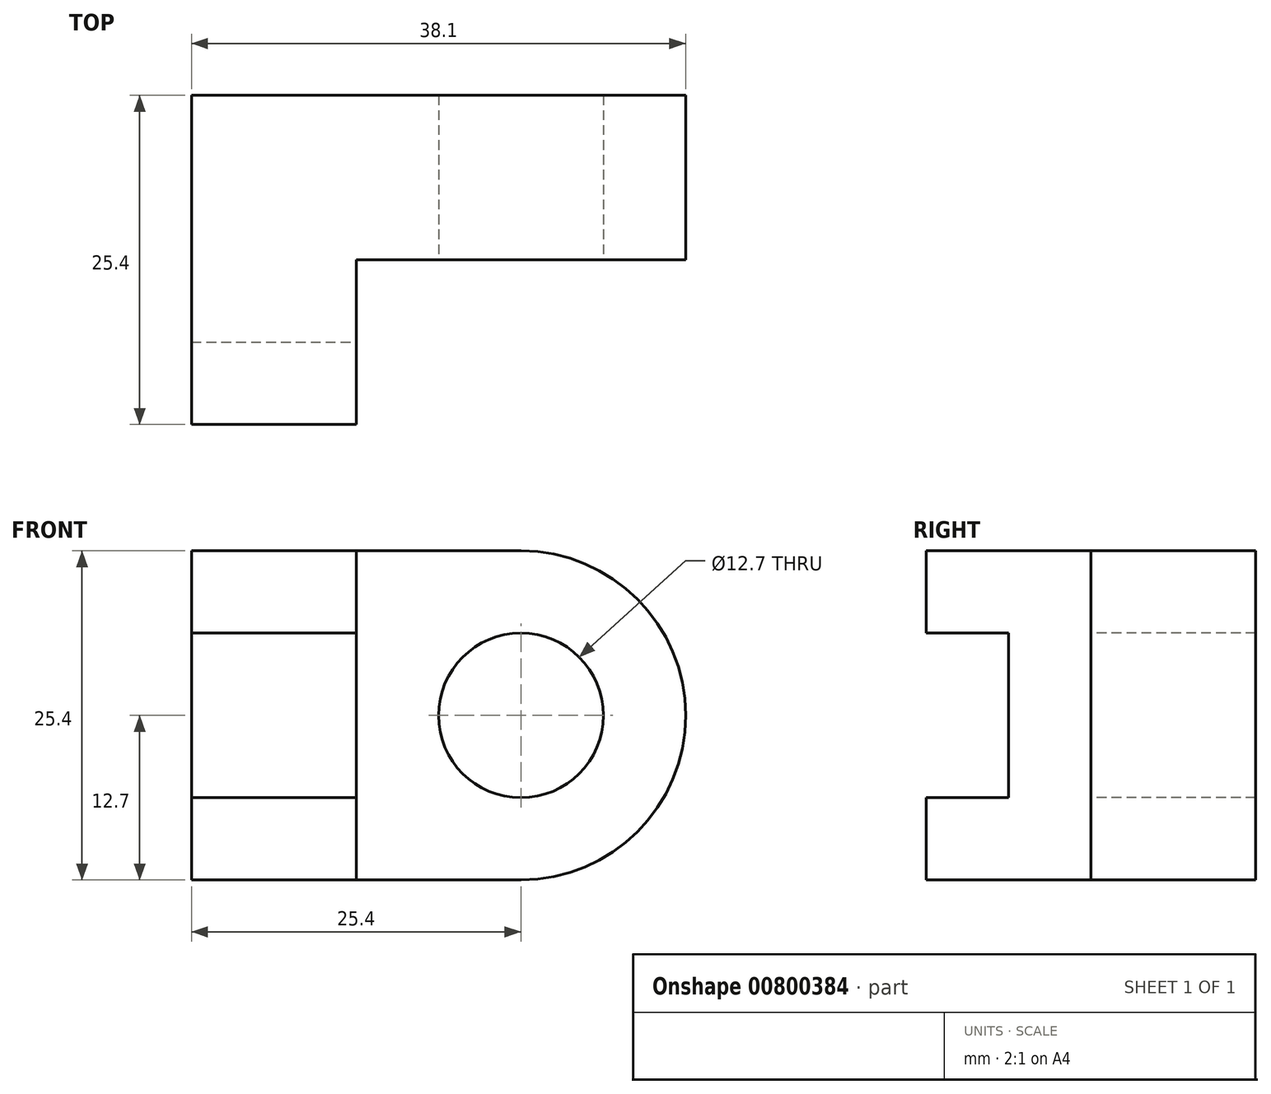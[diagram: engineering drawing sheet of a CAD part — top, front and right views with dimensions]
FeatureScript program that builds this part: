
annotation { "Feature Type Name" : "Feature", "Feature Type Description" : "" }
export const myFeature = defineFeature(function(context is Context, id is Id, definition is map)
    precondition{}
    {
        {
            var Q0;
            Q0=qCreatedBy(makeId("Top.planeOp"),FACE);
            var sketch = newSketch(context, id + "F0", { "sketchPlane" : qUnion([Q0])});
            skLineSegment(sketch, "E0", {"start": v(0, 0) * mm, "end": v(12.7, 0) * mm});
            skLineSegment(sketch, "E1", {"start": v(12.7, 0) * mm, "end": v(12.7, 12.7) * mm});
            skLineSegment(sketch, "E2", {"start": v(0, 0) * mm, "end": v(0, 25.4) * mm});
            skLineSegment(sketch, "E3", {"start": v(0, 25.4) * mm, "end": v(50.8, 25.4) * mm});
            skLineSegment(sketch, "E4", {"start": v(50.8, 25.4) * mm, "end": v(50.8, 12.7) * mm});
            skLineSegment(sketch, "E5", {"start": v(50.8, 12.7) * mm, "end": v(12.7, 12.7) * mm});
            skSolve(sketch);
        }
        {
            var Q0;
            Q0=makeQuery(id+"F0.imprint","IMPRINT",FACE,{"disambiguationData":[TD([[makeQuery(id+"F0.imprint","IMPRINT",EDGE,{"derivedFrom":sQuery(id+"F0.wireOp",EDGE,"E0")}),1.0]])]});
            extrude(context, id + "F1", {"entities" : qUnion([Q0]), "depth" : 25.4 * mm, "offsetDistance" : 25.4 * mm});
        }
        {
            var Q0;
            Q0=makeQuery(id+"F1.opExtrude","SWEPT_FACE",FACE,{"disambiguationData":[OSD([sQuery(id+"F0.wireOp",EDGE,"E1")])]});
            var sketch = newSketch(context, id + "F2", { "sketchPlane" : qUnion([Q0])});
            skLineSegment(sketch, "E6", {"start": v(0, 25.4) * mm, "end": v(0, 19.05) * mm});
            skLineSegment(sketch, "E7", {"start": v(0, 19.05) * mm, "end": v(6.35, 19.05) * mm});
            skLineSegment(sketch, "E8", {"start": v(6.35, 19.05) * mm, "end": v(6.35, 6.35) * mm});
            skLineSegment(sketch, "E9", {"start": v(6.35, 6.35) * mm, "end": v(0, 6.35) * mm});
            skSolve(sketch);
        }
        {
            var Q0;
            {var subQ0=sQuery(id+"F2.wireOp",EDGE,"E7");Q0=makeQuery(id+"F2.imprint","IMPRINT",FACE,{"disambiguationData":[TD([[makeQuery(id+"F2.imprint","IMPRINT",EDGE,{"derivedFrom":subQ0}),-1.0]])]});}
            extrude(context, id + "F3", {"entities" : qUnion([Q0]), "operationType" : NewBodyOperationType.REMOVE, "endBound" : BoundingType.THROUGH_ALL, "oppositeDirection" : true, "depth" : 25.4 * mm, "offsetDistance" : 25.4 * mm});
        }
        {
            var Q0;
            Q0=makeQuery(id+"F1.opExtrude","SWEPT_FACE",FACE,{"disambiguationData":[OSD([sQuery(id+"F0.wireOp",EDGE,"E5")])]});
            var sketch = newSketch(context, id + "F4", { "sketchPlane" : qUnion([Q0])});
            skLineSegment(sketch, "E10", {"start": v(12.7, 25.4) * mm, "end": v(25.4, 25.4) * mm});
            skLineSegment(sketch, "E11", {"start": v(12.7, 0) * mm, "end": v(25.4, 0) * mm});
            skArc(sketch, "E12", {"start": v(25.4, 0) * mm, "mid": v(38.1, 12.7) * mm, "end": v(25.4, 25.4) * mm});
            skCircle(sketch, "E13", {"center": v(25.4, 12.7) * mm, "radius": 6.35 * mm});
            skSolve(sketch);
        }
        {
            var Q0;
            {var subQ0=sQuery(id+"F4.wireOp",EDGE,"E12");Q0=makeQuery(id+"F4.imprint","IMPRINT",FACE,{"disambiguationData":[TD([[makeQuery(id+"F4.imprint","IMPRINT",EDGE,{"derivedFrom":subQ0}),-1.0]])]});}
            var Q1;
            Q1=makeQuery(id+"F4.imprint","IMPRINT",FACE,{"disambiguationData":[TD([[makeQuery(id+"F4.imprint","IMPRINT",EDGE,{"derivedFrom":sQuery(id+"F4.wireOp",EDGE,"E13")}),1.0]])]});
            extrude(context, id + "F5", {"entities" : qUnion([Q0, Q1]), "operationType" : NewBodyOperationType.REMOVE, "endBound" : BoundingType.THROUGH_ALL, "oppositeDirection" : true, "depth" : 25.4 * mm, "offsetDistance" : 25.4 * mm});
        }
    });
